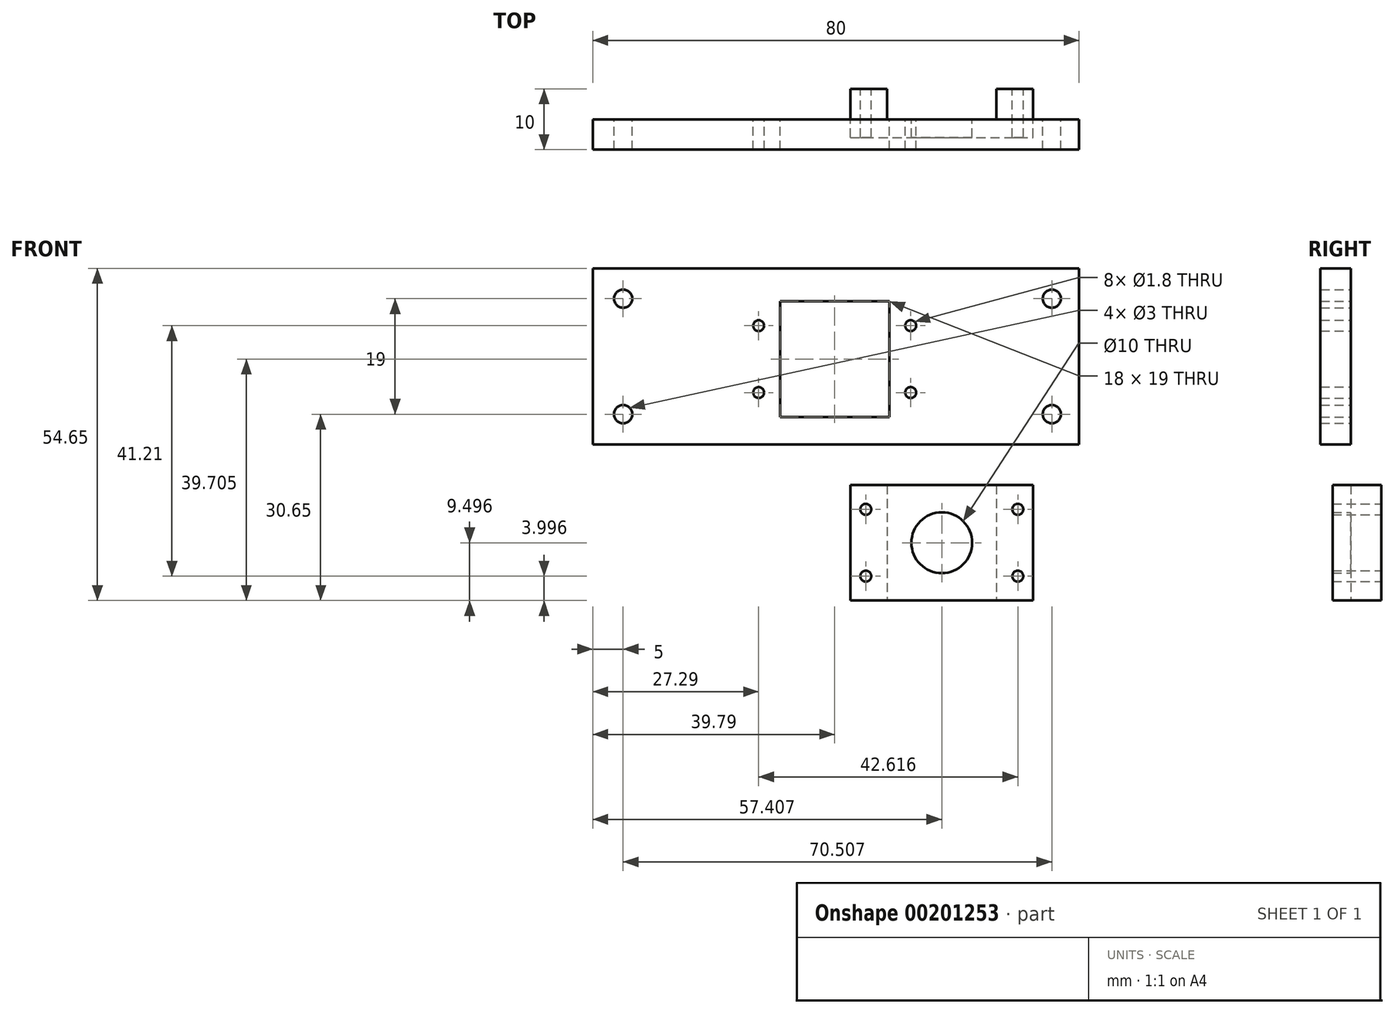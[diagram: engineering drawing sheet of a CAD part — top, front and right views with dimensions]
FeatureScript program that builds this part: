
annotation { "Feature Type Name" : "Feature", "Feature Type Description" : "" }
export const myFeature = defineFeature(function(context is Context, id is Id, definition is map)
    precondition{}
    {
        {
            var Q0;
            Q0=qCreatedBy(makeId("Front.planeOp"),FACE);
            var sketch = newSketch(context, id + "F0", { "sketchPlane" : qUnion([Q0])});
            skLineSegment(sketch, "E0.bottom", {"start": v(40, -14.5) * mm, "end": v(-40, -14.5) * mm});
            skLineSegment(sketch, "E0.top", {"start": v(40, 14.5) * mm, "end": v(-40, 14.5) * mm});
            skLineSegment(sketch, "E0.left", {"start": v(40, -14.5) * mm, "end": v(40, 14.5) * mm});
            skLineSegment(sketch, "E0.right", {"start": v(-40, -14.5) * mm, "end": v(-40, 14.5) * mm});
            skCircle(sketch, "E1", {"center": v(-35, 9.5) * mm, "radius": 1.5 * mm});
            skCircle(sketch, "E2", {"center": v(-35, -9.5) * mm, "radius": 1.5 * mm});
            skLineSegment(sketch, "E3.bottom", {"start": v(-9.2, 9.06) * mm, "end": v(8.8, 9.06) * mm});
            skLineSegment(sketch, "E3.top", {"start": v(-9.2, -9.94) * mm, "end": v(8.8, -9.94) * mm});
            skLineSegment(sketch, "E3.left", {"start": v(-9.2, 9.06) * mm, "end": v(-9.2, -9.94) * mm});
            skLineSegment(sketch, "E3.right", {"start": v(8.8, 9.06) * mm, "end": v(8.8, -9.94) * mm});
            skCircle(sketch, "E4", {"center": v(35.5, 9.5) * mm, "radius": 1.5 * mm});
            skCircle(sketch, "E5", {"center": v(35.5, -9.5) * mm, "radius": 1.5 * mm});
            skCircle(sketch, "E6", {"center": v(-12.7, 5.06) * mm, "radius": 0.9 * mm});
            skCircle(sketch, "E7", {"center": v(-12.7, -5.94) * mm, "radius": 0.9 * mm});
            skCircle(sketch, "E8", {"center": v(12.3, 5.06) * mm, "radius": 0.9 * mm});
            skCircle(sketch, "E9", {"center": v(12.3, -5.94) * mm, "radius": 0.9 * mm});
            skSolve(sketch);
        }
        {
            var Q0;
            Q0 = qSketchRegion(id + "F0", true);
            extrude(context, id + "F1", {"entities" : qUnion([Q0]), "depth" : 5 * mm});
        }
        {
            var Q0;
            Q0=qCreatedBy(makeId("Front.planeOp"),FACE);
            var sketch = newSketch(context, id + "F2", { "sketchPlane" : qUnion([Q0])});
            skLineSegment(sketch, "E10.bottom", {"start": v(8.4, -21.15) * mm, "end": v(26.4, -21.15) * mm});
            skLineSegment(sketch, "E10.top", {"start": v(8.4, -40.15) * mm, "end": v(26.4, -40.15) * mm});
            skLineSegment(sketch, "E10.left", {"start": v(8.4, -21.15) * mm, "end": v(8.4, -40.15) * mm});
            skLineSegment(sketch, "E10.right", {"start": v(26.4, -21.15) * mm, "end": v(26.4, -40.15) * mm});
            skCircle(sketch, "E11", {"center": v(17.4, -30.65) * mm, "radius": 5 * mm});
            skPoint(sketch, "E11.centerSnap0", {"position": v(17.4, -21.15) * mm});
            skPoint(sketch, "E11.centerSnap1", {"position": v(8.4, -30.65) * mm});
            skLineSegment(sketch, "E12.bottom", {"start": v(8.4, -21.15) * mm, "end": v(2.4, -21.15) * mm});
            skLineSegment(sketch, "E12.top", {"start": v(8.4, -40.15) * mm, "end": v(2.4, -40.15) * mm});
            skLineSegment(sketch, "E12.right", {"start": v(2.4, -21.15) * mm, "end": v(2.4, -40.15) * mm});
            skLineSegment(sketch, "E13.bottom", {"start": v(26.4, -21.15) * mm, "end": v(32.4, -21.15) * mm});
            skLineSegment(sketch, "E13.top", {"start": v(26.4, -40.15) * mm, "end": v(32.4, -40.15) * mm});
            skLineSegment(sketch, "E13.right", {"start": v(32.4, -21.15) * mm, "end": v(32.4, -40.15) * mm});
            skCircle(sketch, "E14", {"center": v(4.9, -25.15) * mm, "radius": 0.9 * mm});
            skPoint(sketch, "E14.centerSnap0", {"position": v(5.4, -21.15) * mm});
            skCircle(sketch, "E15", {"center": v(4.9, -36.15) * mm, "radius": 0.9 * mm});
            skCircle(sketch, "E16", {"center": v(29.9, -25.15) * mm, "radius": 0.9 * mm});
            skPoint(sketch, "E16.centerSnap0", {"position": v(29.4, -21.15) * mm});
            skCircle(sketch, "E17", {"center": v(29.9, -36.15) * mm, "radius": 0.9 * mm});
            skSolve(sketch);
        }
        {
            var Q0;
            Q0=makeQuery(id+"F2.imprint","IMPRINT",FACE,{"disambiguationData":[TD([[makeQuery(id+"F2.imprint","IMPRINT",EDGE,{"derivedFrom":sQuery(id+"F2.wireOp",EDGE,"E10.bottom")}),-1.0]])]});
            var Q1;
            Q1=makeQuery(id+"F2.imprint","IMPRINT",FACE,{"disambiguationData":[TD([[makeQuery(id+"F2.imprint","IMPRINT",EDGE,{"derivedFrom":sQuery(id+"F2.wireOp",EDGE,"E12.bottom")}),1.0]])]});
            var Q2;
            Q2=makeQuery(id+"F2.imprint","IMPRINT",FACE,{"disambiguationData":[TD([[makeQuery(id+"F2.imprint","IMPRINT",EDGE,{"derivedFrom":sQuery(id+"F2.wireOp",EDGE,"E13.bottom")}),-1.0]])]});
            extrude(context, id + "F3", {"entities" : qUnion([Q0, Q1, Q2]), "depth" : 3 * mm});
        }
        {
            var Q0;
            Q0=makeQuery(id+"F2.imprint","IMPRINT",FACE,{"disambiguationData":[TD([[makeQuery(id+"F2.imprint","IMPRINT",EDGE,{"derivedFrom":sQuery(id+"F2.wireOp",EDGE,"E12.bottom")}),1.0]])]});
            var Q1;
            Q1=makeQuery(id+"F2.imprint","IMPRINT",FACE,{"disambiguationData":[TD([[makeQuery(id+"F2.imprint","IMPRINT",EDGE,{"derivedFrom":sQuery(id+"F2.wireOp",EDGE,"E13.bottom")}),-1.0]])]});
            extrude(context, id + "F4", {"entities" : qUnion([Q0, Q1]), "operationType" : NewBodyOperationType.ADD, "oppositeDirection" : true, "depth" : 5 * mm});
        }
    });
